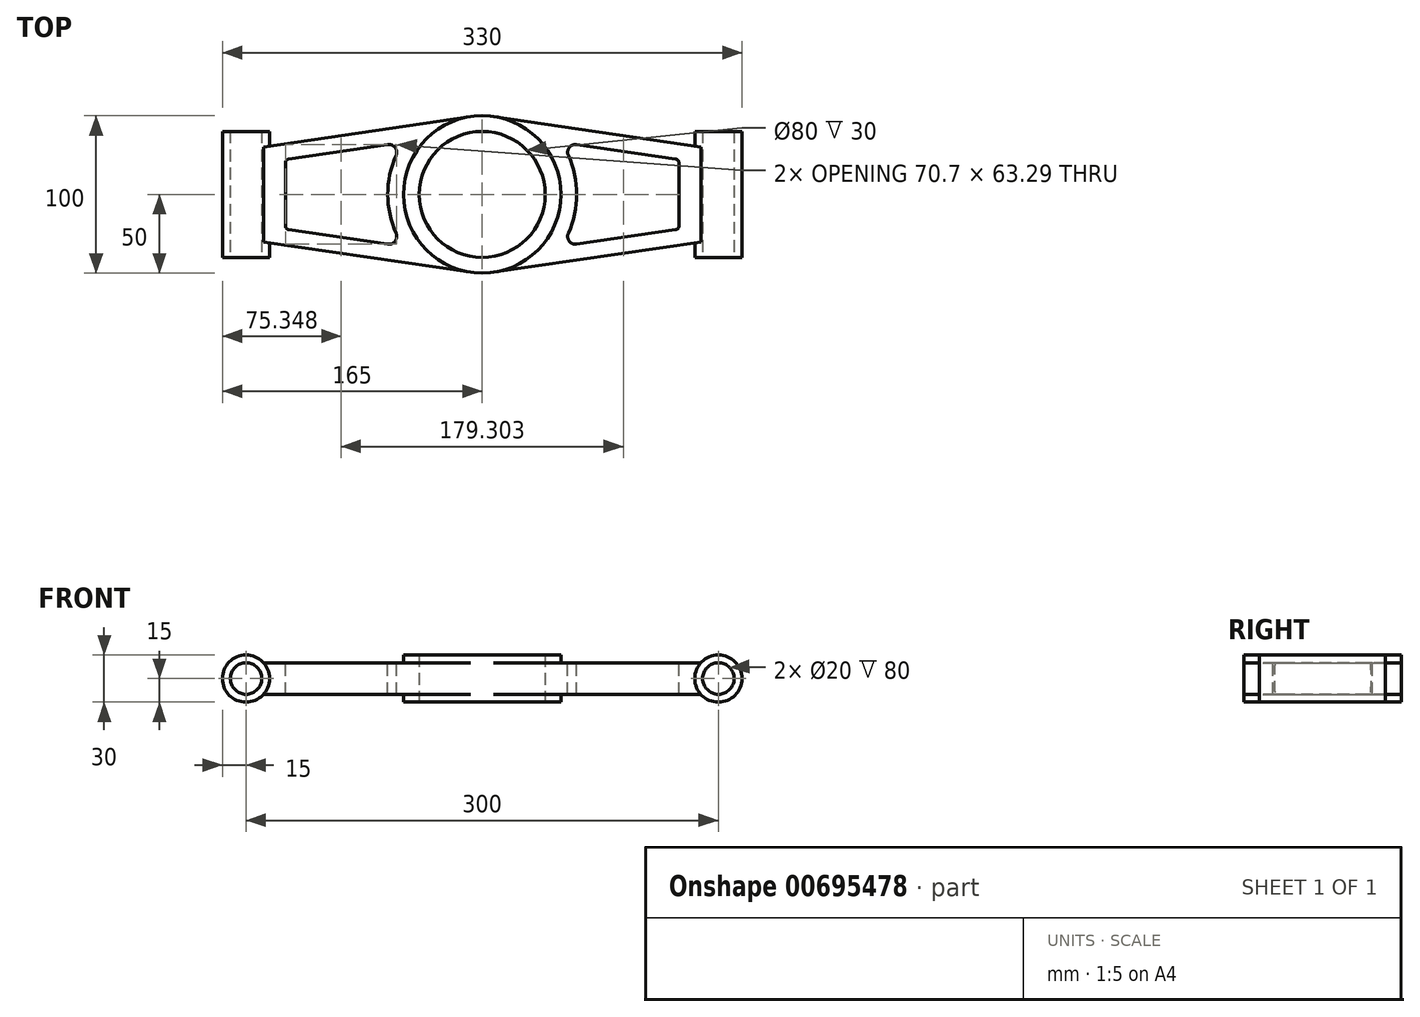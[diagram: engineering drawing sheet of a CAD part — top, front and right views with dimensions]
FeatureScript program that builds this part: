
annotation { "Feature Type Name" : "Feature", "Feature Type Description" : "" }
export const myFeature = defineFeature(function(context is Context, id is Id, definition is map)
    precondition{}
    {
        {
            var Q0;
            Q0=qCreatedBy(makeId("Top.planeOp"),FACE);
            var sketch = newSketch(context, id + "F0", { "sketchPlane" : qUnion([Q0])});
            skArc(sketch, "E0", {"start": v(0, -40) * mm, "mid": v(40, 0) * mm, "end": v(0, 40) * mm});
            skArc(sketch, "E1", {"start": v(0, -50) * mm, "mid": v(50, 0) * mm, "end": v(0, 50) * mm});
            skArc(sketch, "E2", {"start": v(40.07, -44.66) * mm, "mid": v(60, 0) * mm, "end": v(40.07, 44.66) * mm, "construction": true});
            skLineSegment(sketch, "E3", {"start": v(0, 0) * mm, "end": v(140, 0) * mm, "construction": true});
            skLineSegment(sketch, "E4", {"start": v(140, 30) * mm, "end": v(140, -30) * mm});
            skLineSegment(sketch, "E5", {"start": v(140, 30) * mm, "end": v(7.26, 49.47) * mm});
            skLineSegment(sketch, "E6", {"start": v(140, -30) * mm, "end": v(7.26, -49.47) * mm});
            skLineSegment(sketch, "E7", {"start": v(0, 50) * mm, "end": v(0, -50) * mm});
            skSolve(sketch);
        }
        {
            var Q0;
            Q0=makeQuery(id+"F0.imprint","IMPRINT",FACE,{"disambiguationData":[TD([[makeQuery(id+"F0.imprint","IMPRINT",EDGE,{"derivedFrom":sQuery(id+"F0.wireOp",EDGE,"E0")}),-1.0]])]});
            extrude(context, id + "F1", {"entities" : qUnion([Q0]), "depth" : 30 * mm, "offsetDistance" : 25 * mm, "symmetric" : true});
        }
        {
            var Q0;
            Q0 = qSketchRegion(id + "F0", true);
            extrude(context, id + "F2", {"entities" : qUnion([Q0]), "operationType" : NewBodyOperationType.ADD, "depth" : 20 * mm, "offsetDistance" : 25 * mm, "symmetric" : true});
        }
        {
            var Q0;
            {var subQ0=sQuery(id+"F0.wireOp",EDGE,"E0");var subQ1=sQuery(id+"F0.wireOp",EDGE,"E7");var subQ2=sQuery(id+"F0.wireOp",EDGE,"E1");Q0=makeQuery(id+"F2.boolean.opBoolean","SPLIT",FACE,{"disambiguationData":[TD([makeQuery(id+"F1.opExtrude","SWEPT_FACE",FACE,{"disambiguationData":[OSD([subQ0])]})])],"derivedFrom":makeQuery(id+"F2.opExtrude","CAP_FACE",FACE,{"disambiguationData":[OSD([subQ2,sQuery(id+"F0.wireOp",EDGE,"E4"),sQuery(id+"F0.wireOp",EDGE,"E5"),sQuery(id+"F0.wireOp",EDGE,"E6"),subQ1])],"isStart":false})});}
            extrude(context, id + "F3", {"entities" : qUnion([Q0]), "operationType" : NewBodyOperationType.REMOVE, "endBound" : BoundingType.THROUGH_ALL, "oppositeDirection" : true, "depth" : 25 * mm, "offsetDistance" : 25 * mm});
        }
        {
            var Q0;
            Q0=qCreatedBy(makeId("Top.planeOp"),FACE);
            var sketch = newSketch(context, id + "F4", { "sketchPlane" : qUnion([Q0])});
            skArc(sketch, "E8", {"start": v(54.71, -24.63) * mm, "mid": v(60, 0) * mm, "end": v(54.71, 24.63) * mm});
            skLineSegment(sketch, "E9", {"start": v(60, 31.63) * mm, "end": v(122.86, 22.4) * mm});
            skLineSegment(sketch, "E10", {"start": v(122.86, -22.4) * mm, "end": v(60, -31.63) * mm});
            skArc(sketch, "E11", {"start": v(60, 31.63) * mm, "mid": v(55.28, 29.7) * mm, "end": v(54.71, 24.63) * mm});
            skArc(sketch, "E12", {"start": v(54.71, -24.63) * mm, "mid": v(55.28, -29.7) * mm, "end": v(60, -31.63) * mm});
            skArc(sketch, "E13", {"start": v(125, 19.93) * mm, "mid": v(124.4, 21.57) * mm, "end": v(122.86, 22.4) * mm});
            skArc(sketch, "E14", {"start": v(122.86, -22.4) * mm, "mid": v(124.4, -21.57) * mm, "end": v(125, -19.93) * mm});
            skLineSegment(sketch, "E15", {"start": v(125, -19.93) * mm, "end": v(125, 19.93) * mm});
            skSolve(sketch);
        }
        {
            var Q0;
            Q0 = qSketchRegion(id + "F4", true);
            extrude(context, id + "F5", {"entities" : qUnion([Q0]), "operationType" : NewBodyOperationType.REMOVE, "endBound" : BoundingType.THROUGH_ALL, "oppositeDirection" : true, "depth" : 25 * mm, "offsetDistance" : 25 * mm, "hasSecondDirection" : true, "secondDirectionBound" : BoundingType.THROUGH_ALL, "secondDirectionOppositeDirection" : false, "secondDirectionDepth" : 25 * mm});
        }
        {
            var Q0;
            Q0=qCreatedBy(makeId("Front.planeOp"),FACE);
            var sketch = newSketch(context, id + "F6", { "sketchPlane" : qUnion([Q0])});
            skCircle(sketch, "E16", {"center": v(150, 0) * mm, "radius": 15 * mm});
            skSolve(sketch);
        }
        {
            var Q0;
            Q0=makeQuery(id+"F6.imprint","IMPRINT",FACE,{"disambiguationData":[TD([[makeQuery(id+"F6.imprint","IMPRINT",EDGE,{"derivedFrom":sQuery(id+"F6.wireOp",EDGE,"E16")}),1.0]])]});
            extrude(context, id + "F7", {"entities" : qUnion([Q0]), "operationType" : NewBodyOperationType.ADD, "depth" : 80 * mm, "offsetDistance" : 25 * mm, "symmetric" : true});
        }
        {
            var Q0;
            Q0=makeQuery(id+"F7.opExtrude","CAP_FACE",FACE,{"disambiguationData":[OSD([sQuery(id+"F6.wireOp",EDGE,"E16")])],"isStart":false});
            var sketch = newSketch(context, id + "F8", { "sketchPlane" : qUnion([Q0])});
            skCircle(sketch, "E17", {"center": v(150, 0) * mm, "radius": 10 * mm});
            skSolve(sketch);
        }
        {
            var Q0;
            Q0=makeQuery(id+"F8.imprint","IMPRINT",FACE,{"disambiguationData":[TD([[makeQuery(id+"F8.imprint","IMPRINT",EDGE,{"derivedFrom":sQuery(id+"F8.wireOp",EDGE,"E17")}),1.0]])]});
            extrude(context, id + "F9", {"entities" : qUnion([Q0]), "operationType" : NewBodyOperationType.REMOVE, "endBound" : BoundingType.THROUGH_ALL, "oppositeDirection" : true, "depth" : 25 * mm, "offsetDistance" : 25 * mm});
        }
        {
            var Q0;
            Q0=makeQuery(id+"F1.opExtrude","SWEPT_BODY",BODY,{"disambiguationData":[OSD([sQuery(id+"F0.wireOp",EDGE,"E0"),sQuery(id+"F0.wireOp",EDGE,"E1"),sQuery(id+"F0.wireOp",EDGE,"E7")])]});
            var Q1;
            Q1=qCreatedBy(makeId("Right.planeOp"),FACE);
            mirror(context, id + "F10", {"operationType" : NewBodyOperationType.ADD, "entities" : qUnion([Q0]), "mirrorPlane" : qUnion([Q1])});
        }
    });
